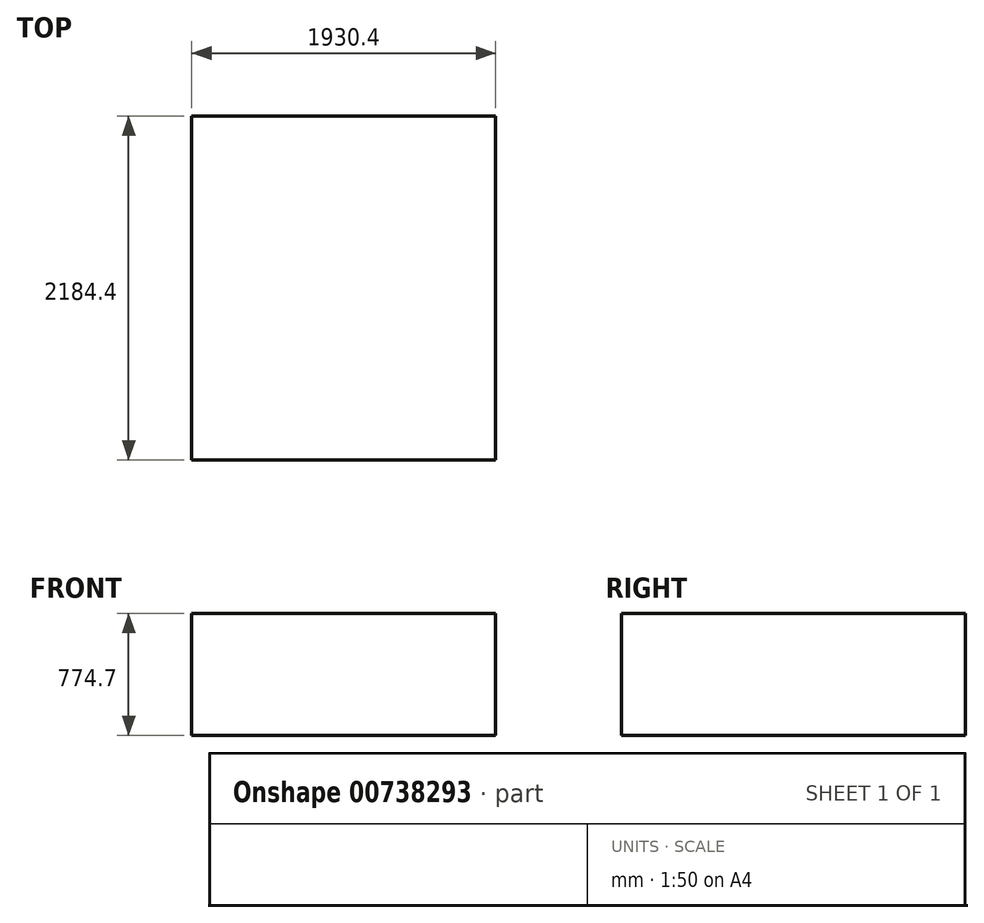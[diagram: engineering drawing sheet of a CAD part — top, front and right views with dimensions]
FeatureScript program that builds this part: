
annotation { "Feature Type Name" : "Feature", "Feature Type Description" : "" }
export const myFeature = defineFeature(function(context is Context, id is Id, definition is map)
    precondition{}
    {
        {
            var Q0;
            Q0=qCreatedBy(makeId("Top.planeOp"),FACE);
            var sketch = newSketch(context, id + "F0", { "sketchPlane" : qUnion([Q0])});
            skLineSegment(sketch, "E0.bottom", {"start": v(965.2, 1092.2) * mm, "end": v(-965.2, 1092.2) * mm});
            skLineSegment(sketch, "E0.top", {"start": v(965.2, -1092.2) * mm, "end": v(-965.2, -1092.2) * mm});
            skLineSegment(sketch, "E0.left", {"start": v(965.2, 1092.2) * mm, "end": v(965.2, -1092.2) * mm});
            skLineSegment(sketch, "E0.right", {"start": v(-965.2, 1092.2) * mm, "end": v(-965.2, -1092.2) * mm});
            skPoint(sketch, "E0.middle", {"position": v(0, 0) * mm});
            skSolve(sketch);
        }
        {
            var Q0;
            Q0=makeQuery(id+"F0.imprint","IMPRINT",FACE,{"disambiguationData":[TD([[makeQuery(id+"F0.imprint","IMPRINT",EDGE,{"derivedFrom":sQuery(id+"F0.wireOp",EDGE,"E0.bottom")}),1.0]])]});
            extrude(context, id + "F1", {"entities" : qUnion([Q0]), "oppositeDirection" : true, "depth" : 774.7 * mm, "offsetDistance" : 25.4 * mm});
        }
    });
